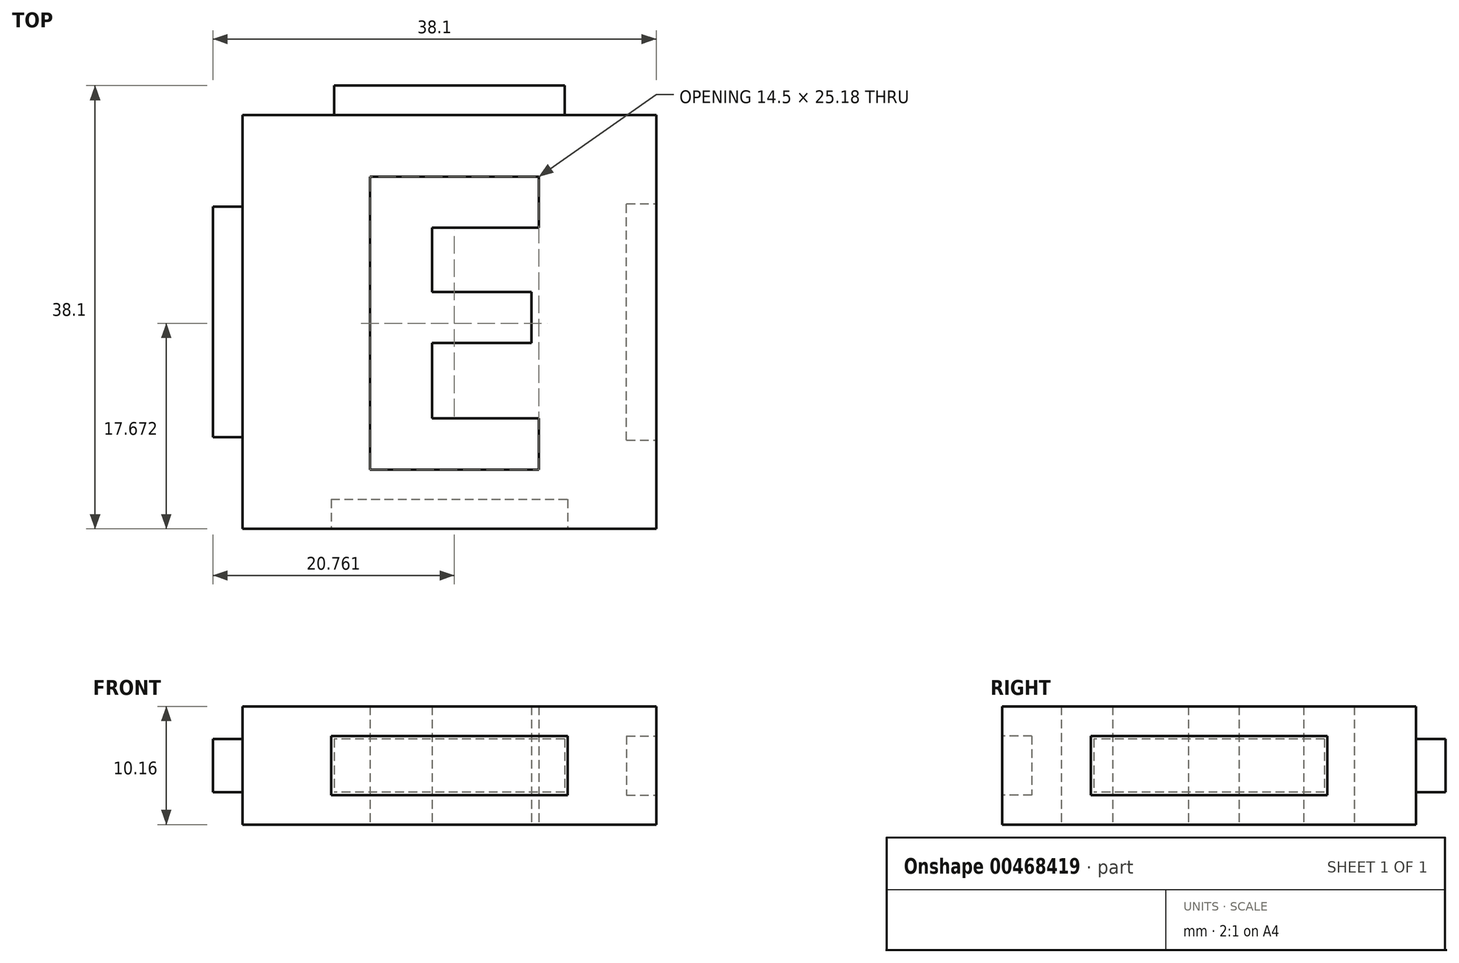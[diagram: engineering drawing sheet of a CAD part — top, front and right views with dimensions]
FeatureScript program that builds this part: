
annotation { "Feature Type Name" : "Feature", "Feature Type Description" : "" }
export const myFeature = defineFeature(function(context is Context, id is Id, definition is map)
    precondition{}
    {
        {
            var Q0;
            Q0=qCreatedBy(makeId("Top.planeOp"),FACE);
            var sketch = newSketch(context, id + "F0", { "sketchPlane" : qUnion([Q0])});
            skLineSegment(sketch, "E0.bottom", {"start": v(-17.78, 17.78) * mm, "end": v(17.78, 17.78) * mm});
            skLineSegment(sketch, "E0.top", {"start": v(-17.78, -17.78) * mm, "end": v(17.78, -17.78) * mm});
            skLineSegment(sketch, "E0.left", {"start": v(-17.78, 17.78) * mm, "end": v(-17.78, -17.78) * mm});
            skLineSegment(sketch, "E0.right", {"start": v(17.78, 17.78) * mm, "end": v(17.78, -17.78) * mm});
            skText(sketch, "E1", { "text": "E", "fontName": "OpenSans-Bold.ttf"});
            const initialGuessF0  = {"E1": [-0.00998, -0.0127, 1, 0, 0.0254]};
            skSetInitialGuess(sketch, initialGuessF0);
            skSolve(sketch);
        }
        {
            var Q0;
            Q0=qSketchRegion(id+"F0",true);
            extrude(context, id + "F1", {"entities" : qUnion([Q0]), "endBound" : BoundingType.SYMMETRIC, "depth" : 10.16 * mm});
        }
        {
            var Q0;
            Q0=makeQuery(id+"F1.opExtrude","SWEPT_FACE",FACE,{"disambiguationData":[OSD([sQuery(id+"F0.wireOp",EDGE,"E0.bottom")])]});
            var sketch = newSketch(context, id + "F2", { "sketchPlane" : qUnion([Q0])});
            skLineSegment(sketch, "E2.bottom", {"start": v(-9.9, 2.29) * mm, "end": v(9.9, 2.29) * mm});
            skLineSegment(sketch, "E2.top", {"start": v(-9.9, -2.29) * mm, "end": v(9.9, -2.29) * mm});
            skLineSegment(sketch, "E2.left", {"start": v(-9.9, 2.29) * mm, "end": v(-9.9, -2.29) * mm});
            skLineSegment(sketch, "E2.right", {"start": v(9.9, 2.29) * mm, "end": v(9.9, -2.29) * mm});
            skSolve(sketch);
        }
        {
            var Q0;
            Q0=qSketchRegion(id+"F2",true);
            extrude(context, id + "F3", {"entities" : qUnion([Q0]), "operationType" : NewBodyOperationType.ADD, "depth" : 2.54 * mm});
        }
        {
            var Q0;
            Q0=makeQuery(id+"F1.opExtrude","SWEPT_FACE",FACE,{"disambiguationData":[OSD([sQuery(id+"F0.wireOp",EDGE,"E0.left")])]});
            var sketch = newSketch(context, id + "F4", { "sketchPlane" : qUnion([Q0])});
            skLineSegment(sketch, "E3.bottom", {"start": v(-9.9, 2.29) * mm, "end": v(9.9, 2.29) * mm});
            skLineSegment(sketch, "E3.top", {"start": v(-9.9, -2.29) * mm, "end": v(9.9, -2.29) * mm});
            skLineSegment(sketch, "E3.left", {"start": v(-9.9, 2.29) * mm, "end": v(-9.9, -2.29) * mm});
            skLineSegment(sketch, "E3.right", {"start": v(9.9, 2.29) * mm, "end": v(9.9, -2.29) * mm});
            skSolve(sketch);
        }
        {
            var Q0;
            Q0=qSketchRegion(id+"F4",true);
            extrude(context, id + "F5", {"entities" : qUnion([Q0]), "operationType" : NewBodyOperationType.ADD, "depth" : 2.54 * mm});
        }
        {
            var Q0;
            Q0=makeQuery(id+"F1.opExtrude","SWEPT_FACE",FACE,{"disambiguationData":[OSD([sQuery(id+"F0.wireOp",EDGE,"E0.top")])]});
            var sketch = newSketch(context, id + "F6", { "sketchPlane" : qUnion([Q0])});
            skLineSegment(sketch, "E4.bottom", {"start": v(-10.16, 2.54) * mm, "end": v(10.16, 2.54) * mm});
            skLineSegment(sketch, "E4.top", {"start": v(-10.16, -2.54) * mm, "end": v(10.16, -2.54) * mm});
            skLineSegment(sketch, "E4.left", {"start": v(-10.16, 2.54) * mm, "end": v(-10.16, -2.54) * mm});
            skLineSegment(sketch, "E4.right", {"start": v(10.16, 2.54) * mm, "end": v(10.16, -2.54) * mm});
            skSolve(sketch);
        }
        {
            var Q0;
            Q0=qSketchRegion(id+"F6",true);
            extrude(context, id + "F7", {"entities" : qUnion([Q0]), "operationType" : NewBodyOperationType.REMOVE, "oppositeDirection" : true, "depth" : 2.54 * mm});
        }
        {
            var Q0;
            Q0=makeQuery(id+"F1.opExtrude","SWEPT_FACE",FACE,{"disambiguationData":[OSD([sQuery(id+"F0.wireOp",EDGE,"E0.right")])]});
            var sketch = newSketch(context, id + "F8", { "sketchPlane" : qUnion([Q0])});
            skLineSegment(sketch, "E5.bottom", {"start": v(-10.16, 2.54) * mm, "end": v(10.16, 2.54) * mm});
            skLineSegment(sketch, "E5.top", {"start": v(-10.16, -2.54) * mm, "end": v(10.16, -2.54) * mm});
            skLineSegment(sketch, "E5.left", {"start": v(-10.16, 2.54) * mm, "end": v(-10.16, -2.54) * mm});
            skLineSegment(sketch, "E5.right", {"start": v(10.16, 2.54) * mm, "end": v(10.16, -2.54) * mm});
            skSolve(sketch);
        }
        {
            var Q0;
            Q0=qSketchRegion(id+"F8",true);
            extrude(context, id + "F9", {"entities" : qUnion([Q0]), "operationType" : NewBodyOperationType.REMOVE, "oppositeDirection" : true, "depth" : 2.54 * mm});
        }
    });
